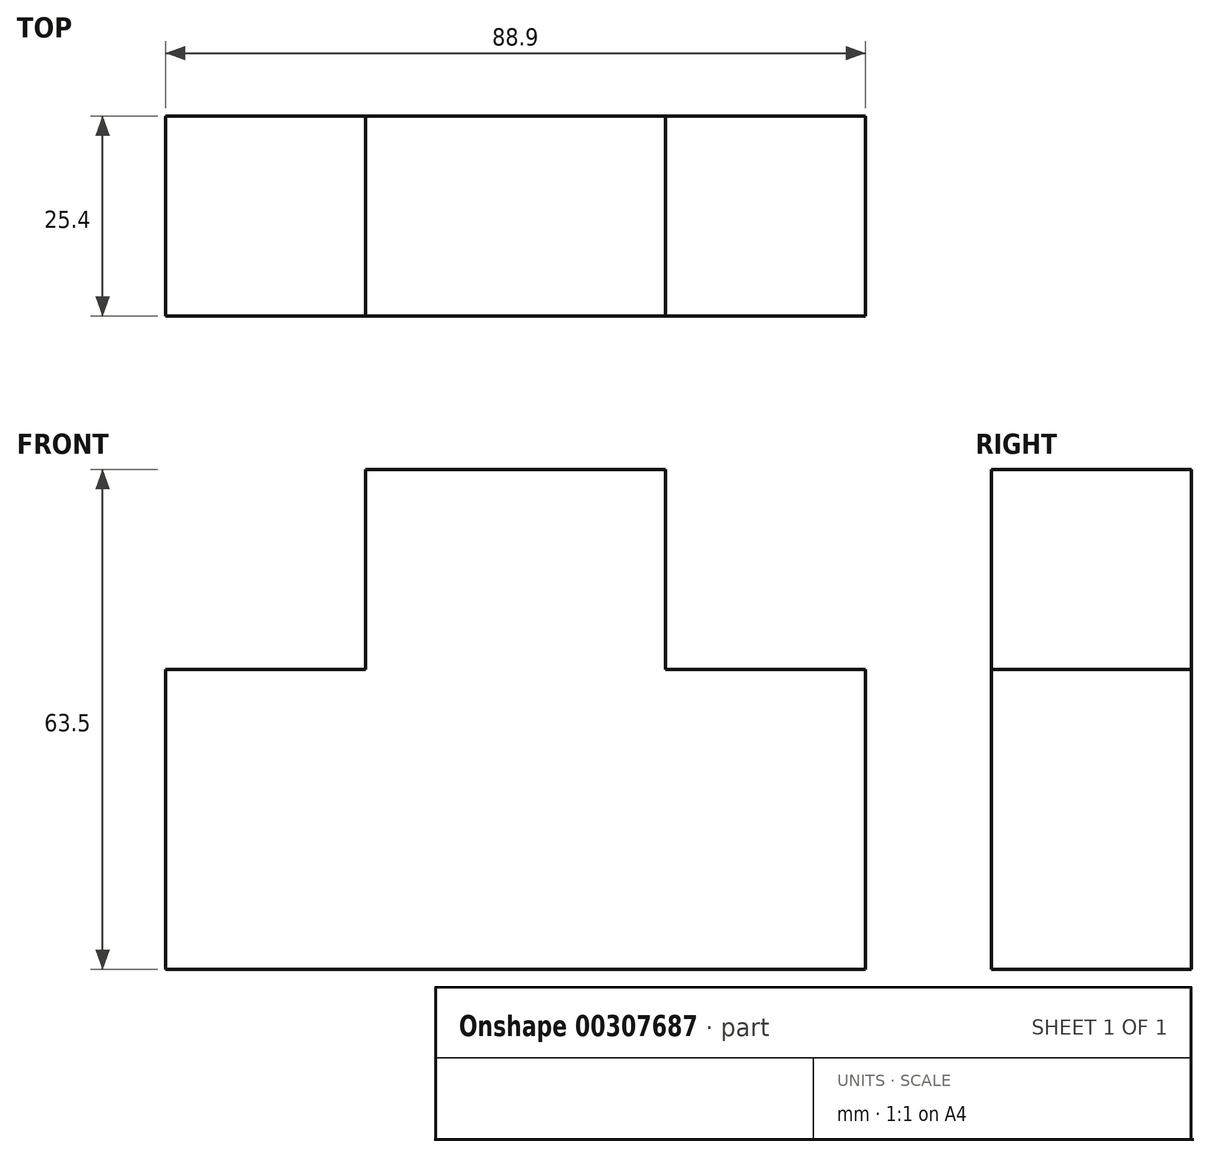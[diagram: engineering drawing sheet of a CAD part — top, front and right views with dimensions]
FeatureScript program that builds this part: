
annotation { "Feature Type Name" : "Feature", "Feature Type Description" : "" }
export const myFeature = defineFeature(function(context is Context, id is Id, definition is map)
    precondition{}
    {
        {
            var Q0;
            Q0=qCreatedBy(makeId("Front.planeOp"),FACE);
            var sketch = newSketch(context, id + "F0", { "sketchPlane" : qUnion([Q0])});
            skLineSegment(sketch, "E0", {"start": v(-39.66, -63.5) * mm, "end": v(49.24, -63.5) * mm});
            skLineSegment(sketch, "E1", {"start": v(49.24, -63.5) * mm, "end": v(49.24, -25.4) * mm});
            skLineSegment(sketch, "E2", {"start": v(49.24, -25.4) * mm, "end": v(23.84, -25.4) * mm});
            skLineSegment(sketch, "E3", {"start": v(23.84, -25.4) * mm, "end": v(23.84, 0) * mm});
            skLineSegment(sketch, "E4", {"start": v(23.84, 0) * mm, "end": v(-14.26, 0) * mm});
            skLineSegment(sketch, "E5", {"start": v(-14.26, 0) * mm, "end": v(-14.26, -25.4) * mm});
            skLineSegment(sketch, "E6", {"start": v(-14.26, -25.4) * mm, "end": v(-39.66, -25.4) * mm});
            skLineSegment(sketch, "E7", {"start": v(-39.66, -25.4) * mm, "end": v(-39.66, -63.5) * mm});
            skSolve(sketch);
        }
        {
            var Q0;
            Q0=makeQuery(id+"F0.imprint","IMPRINT",FACE,{"disambiguationData":[TD([[makeQuery(id+"F0.imprint","IMPRINT",EDGE,{"derivedFrom":sQuery(id+"F0.wireOp",EDGE,"E0")}),1.0]])]});
            extrude(context, id + "F1", {"entities" : qUnion([Q0]), "depth" : 25.4 * mm});
        }
    });
